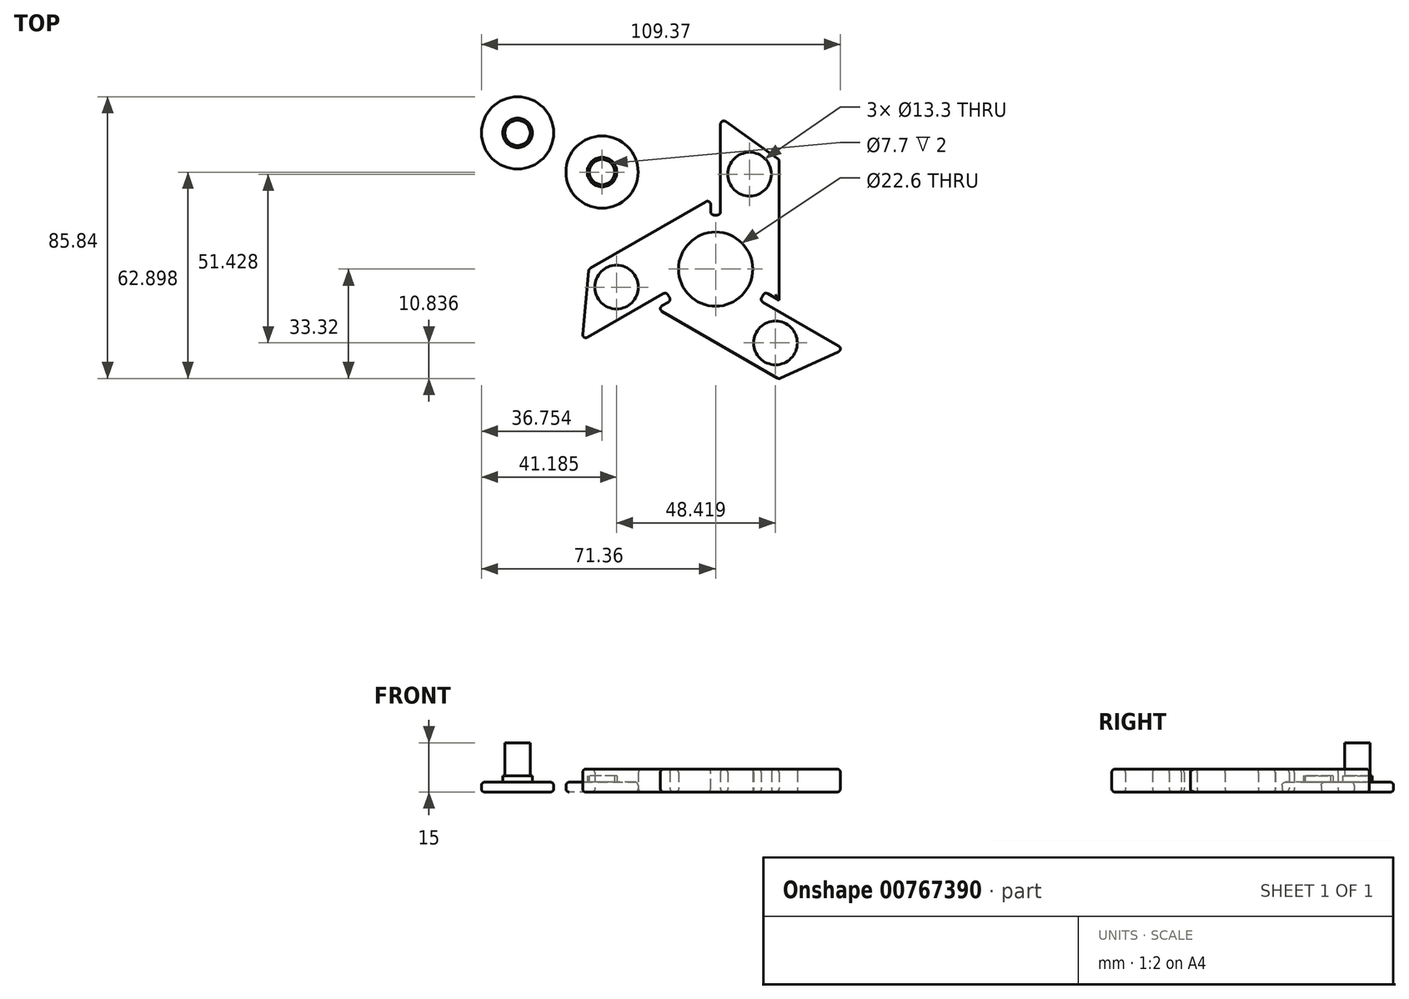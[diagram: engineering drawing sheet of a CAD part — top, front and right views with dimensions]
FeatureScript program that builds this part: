
annotation { "Feature Type Name" : "Feature", "Feature Type Description" : "" }
export const myFeature = defineFeature(function(context is Context, id is Id, definition is map)
    precondition{}
    {
        {
            var Q0;
            Q0=qCreatedBy(makeId("Top.planeOp"),FACE);
            var sketch = newSketch(context, id + "F0", { "sketchPlane" : qUnion([Q0])});
            skCircle(sketch, "E0", {"center": v(0, 0) * mm, "radius": 11.3 * mm});
            skCircle(sketch, "E1", {"center": v(0, 0) * mm, "radius": 16.5 * mm});
            skLineSegment(sketch, "E2", {"start": v(0, 74) * mm, "end": v(0, -68.77) * mm, "construction": true});
            skLineSegment(sketch, "E3", {"start": v(0, 0) * mm, "end": v(71.6, -41.34) * mm, "construction": true});
            skLineSegment(sketch, "E4", {"start": v(0, 0) * mm, "end": v(-62.65, -36.17) * mm, "construction": true});
            skLineSegment(sketch, "E5", {"start": v(-1.5, 16.43) * mm, "end": v(-1.5, 21.43) * mm});
            skLineSegment(sketch, "E6", {"start": v(1.5, 16.43) * mm, "end": v(1.5, 21.43) * mm});
            skLineSegment(sketch, "E7", {"start": v(13.48, -9.51) * mm, "end": v(17.81, -12.01) * mm});
            skLineSegment(sketch, "E8", {"start": v(14.98, -6.92) * mm, "end": v(19.31, -9.42) * mm});
            skLineSegment(sketch, "E9", {"start": v(-13.48, -9.51) * mm, "end": v(-17.81, -12.01) * mm});
            skLineSegment(sketch, "E10", {"start": v(-14.98, -6.92) * mm, "end": v(-19.31, -9.42) * mm});
            skLineSegment(sketch, "E11", {"start": v(-1.5, 21.43) * mm, "end": v(-38.62, 0) * mm});
            skLineSegment(sketch, "E12", {"start": v(-38.62, 0) * mm, "end": v(-40.7, -21.76) * mm});
            skLineSegment(sketch, "E13", {"start": v(-40.7, -21.76) * mm, "end": v(-19.31, -9.42) * mm});
            skLineSegment(sketch, "E14", {"start": v(-17.81, -12.01) * mm, "end": v(19.31, -33.45) * mm});
            skLineSegment(sketch, "E15", {"start": v(19.31, -33.45) * mm, "end": v(39.2, -24.36) * mm});
            skLineSegment(sketch, "E16", {"start": v(39.2, -24.36) * mm, "end": v(17.81, -12.01) * mm});
            skLineSegment(sketch, "E17", {"start": v(19.31, -9.42) * mm, "end": v(19.31, 33.45) * mm});
            skLineSegment(sketch, "E18", {"start": v(19.31, 33.45) * mm, "end": v(1.5, 46.12) * mm});
            skLineSegment(sketch, "E19", {"start": v(1.5, 46.12) * mm, "end": v(1.5, 21.43) * mm});
            skCircle(sketch, "E20", {"center": v(-30.18, -5.47) * mm, "radius": 6.65 * mm});
            skCircle(sketch, "E21", {"center": v(18.24, -22.48) * mm, "radius": 6.65 * mm});
            skCircle(sketch, "E22", {"center": v(10.35, 28.94) * mm, "radius": 6.65 * mm});
            skCircle(sketch, "E23", {"center": v(-60.36, 41.52) * mm, "radius": 11 * mm});
            skCircle(sketch, "E24", {"center": v(-34.6, 29.58) * mm, "radius": 11 * mm});
            skSolve(sketch);
        }
        {
            var Q0;
            {var subQ1=sQuery(id+"F0.wireOp",EDGE,"E7");Q0=makeQuery(id+"F0.imprint","IMPRINT",FACE,{"disambiguationData":[TD([[makeQuery(id+"F0.imprint","IMPRINT",EDGE,{"derivedFrom":subQ1}),-1.0]])]});}
            var Q1;
            {var subQ0=sQuery(id+"F0.wireOp",EDGE,"E5");Q1=makeQuery(id+"F0.imprint","IMPRINT",FACE,{"disambiguationData":[TD([[makeQuery(id+"F0.imprint","IMPRINT",EDGE,{"derivedFrom":subQ0}),1.0]])]});}
            var Q2;
            {var subQ0=sQuery(id+"F0.wireOp",EDGE,"E6");Q2=makeQuery(id+"F0.imprint","IMPRINT",FACE,{"disambiguationData":[TD([[makeQuery(id+"F0.imprint","IMPRINT",EDGE,{"derivedFrom":subQ0}),-1.0]])]});}
            var Q3;
            Q3=makeQuery(id+"F0.imprint","IMPRINT",FACE,{"disambiguationData":[TD([[makeQuery(id+"F0.imprint","IMPRINT",EDGE,{"derivedFrom":sQuery(id+"F0.wireOp",EDGE,"E0")}),-1.0]])]});
            extrude(context, id + "F1", {"entities" : qUnion([Q0, Q1, Q2, Q3]), "depth" : 7 * mm, "offsetDistance" : 25 * mm});
        }
        {
            var Q0;
            Q0=makeQuery(id+"F1.opExtrude","CAP_EDGE",EDGE,{"disambiguationData":[OSD([sQuery(id+"F0.wireOp",EDGE,"E17")])],"isStart":false});
            var Q1;
            Q1=makeQuery(id+"F1.opExtrude","CAP_EDGE",EDGE,{"disambiguationData":[OSD([sQuery(id+"F0.wireOp",EDGE,"E18")])],"isStart":false});
            var Q2;
            Q2=makeQuery(id+"F1.opExtrude","CAP_EDGE",EDGE,{"disambiguationData":[OSD([sQuery(id+"F0.wireOp",EDGE,"E6"),sQuery(id+"F0.wireOp",EDGE,"E19")])],"isStart":false});
            var Q3;
            Q3=makeQuery(id+"F1.opExtrude","CAP_EDGE",EDGE,{"disambiguationData":[OSD([sQuery(id+"F0.wireOp",EDGE,"E11")])],"isStart":false});
            var Q4;
            Q4=makeQuery(id+"F1.opExtrude","CAP_EDGE",EDGE,{"disambiguationData":[OSD([sQuery(id+"F0.wireOp",EDGE,"E5")])],"isStart":false});
            var Q5;
            {var subQ0=sQuery(id+"F0.wireOp",EDGE,"E1");Q5=makeQuery(id+"F1.opExtrude","CAP_EDGE",EDGE,{"disambiguationData":[OSD([subQ0]),TDD([makeQuery(id+"F0.imprint","IMPRINT",EDGE,{"disambiguationData":[TD([[makeQuery(id+"F0.imprint","INTERSECT",VERTEX,{"derivedFrom":[subQ0,sQuery(id+"F0.wireOp",EDGE,"E5")]}),1.0]])],"derivedFrom":subQ0})])],"isStart":false});}
            var Q6;
            Q6=makeQuery(id+"F1.opExtrude","CAP_EDGE",EDGE,{"disambiguationData":[OSD([sQuery(id+"F0.wireOp",EDGE,"E12")])],"isStart":false});
            var Q7;
            Q7=makeQuery(id+"F1.opExtrude","CAP_EDGE",EDGE,{"disambiguationData":[OSD([sQuery(id+"F0.wireOp",EDGE,"E10"),sQuery(id+"F0.wireOp",EDGE,"E13")])],"isStart":false});
            var Q8;
            {var subQ0=sQuery(id+"F0.wireOp",EDGE,"E1");Q8=makeQuery(id+"F1.opExtrude","CAP_EDGE",EDGE,{"disambiguationData":[OSD([subQ0]),TDD([makeQuery(id+"F0.imprint","IMPRINT",EDGE,{"disambiguationData":[TD([[makeQuery(id+"F0.imprint","INTERSECT",VERTEX,{"derivedFrom":[subQ0,sQuery(id+"F0.wireOp",EDGE,"E9")]}),1.0]])],"derivedFrom":subQ0})])],"isStart":false});}
            var Q9;
            Q9=makeQuery(id+"F1.opExtrude","CAP_EDGE",EDGE,{"disambiguationData":[OSD([sQuery(id+"F0.wireOp",EDGE,"E9")])],"isStart":false});
            var Q10;
            Q10=makeQuery(id+"F1.opExtrude","CAP_EDGE",EDGE,{"disambiguationData":[OSD([sQuery(id+"F0.wireOp",EDGE,"E14")])],"isStart":false});
            var Q11;
            Q11=makeQuery(id+"F1.opExtrude","CAP_EDGE",EDGE,{"disambiguationData":[OSD([sQuery(id+"F0.wireOp",EDGE,"E15")])],"isStart":false});
            var Q12;
            Q12=makeQuery(id+"F1.opExtrude","CAP_EDGE",EDGE,{"disambiguationData":[OSD([sQuery(id+"F0.wireOp",EDGE,"E7"),sQuery(id+"F0.wireOp",EDGE,"E16")])],"isStart":false});
            var Q13;
            Q13=makeQuery(id+"F1.opExtrude","CAP_EDGE",EDGE,{"disambiguationData":[OSD([sQuery(id+"F0.wireOp",EDGE,"E8")])],"isStart":false});
            var Q14;
            Q14=makeQuery(id+"F1.opExtrude","CAP_EDGE",EDGE,{"disambiguationData":[OSD([sQuery(id+"F0.wireOp",EDGE,"E15")])],"isStart":true});
            var Q15;
            Q15=makeQuery(id+"F1.opExtrude","CAP_EDGE",EDGE,{"disambiguationData":[OSD([sQuery(id+"F0.wireOp",EDGE,"E14")])],"isStart":true});
            var Q16;
            Q16=makeQuery(id+"F1.opExtrude","SWEPT_EDGE",EDGE,{"disambiguationData":[OSD([sQuery(id+"F0.wireOp",EDGE,"E14"),sQuery(id+"F0.wireOp",EDGE,"E15")])]});
            var Q17;
            Q17=makeQuery(id+"F1.opExtrude","SWEPT_EDGE",EDGE,{"disambiguationData":[OSD([sQuery(id+"F0.wireOp",EDGE,"E15"),sQuery(id+"F0.wireOp",EDGE,"E16")])]});
            var Q18;
            Q18=makeQuery(id+"F1.opExtrude","SWEPT_EDGE",EDGE,{"disambiguationData":[OSD([sQuery(id+"F0.wireOp",EDGE,"E9"),sQuery(id+"F0.wireOp",EDGE,"E14")])]});
            var Q19;
            Q19=makeQuery(id+"F1.opExtrude","SWEPT_EDGE",EDGE,{"disambiguationData":[OSD([sQuery(id+"F0.wireOp",EDGE,"E1"),sQuery(id+"F0.wireOp",EDGE,"E10")])]});
            var Q20;
            Q20=makeQuery(id+"F1.opExtrude","SWEPT_EDGE",EDGE,{"disambiguationData":[OSD([sQuery(id+"F0.wireOp",EDGE,"E1"),sQuery(id+"F0.wireOp",EDGE,"E9")])]});
            var Q21;
            Q21=makeQuery(id+"F1.opExtrude","CAP_EDGE",EDGE,{"disambiguationData":[OSD([sQuery(id+"F0.wireOp",EDGE,"E10"),sQuery(id+"F0.wireOp",EDGE,"E13")])],"isStart":true});
            var Q22;
            Q22=makeQuery(id+"F1.opExtrude","SWEPT_EDGE",EDGE,{"disambiguationData":[OSD([sQuery(id+"F0.wireOp",EDGE,"E12"),sQuery(id+"F0.wireOp",EDGE,"E13")])]});
            var Q23;
            Q23=makeQuery(id+"F1.opExtrude","CAP_EDGE",EDGE,{"disambiguationData":[OSD([sQuery(id+"F0.wireOp",EDGE,"E12")])],"isStart":true});
            var Q24;
            Q24=makeQuery(id+"F1.opExtrude","SWEPT_EDGE",EDGE,{"disambiguationData":[OSD([sQuery(id+"F0.wireOp",EDGE,"E11"),sQuery(id+"F0.wireOp",EDGE,"E12")])]});
            var Q25;
            Q25=makeQuery(id+"F1.opExtrude","CAP_EDGE",EDGE,{"disambiguationData":[OSD([sQuery(id+"F0.wireOp",EDGE,"E11")])],"isStart":true});
            var Q26;
            Q26=makeQuery(id+"F1.opExtrude","SWEPT_EDGE",EDGE,{"disambiguationData":[OSD([sQuery(id+"F0.wireOp",EDGE,"E5"),sQuery(id+"F0.wireOp",EDGE,"E11")])]});
            var Q27;
            Q27=makeQuery(id+"F1.opExtrude","SWEPT_EDGE",EDGE,{"disambiguationData":[OSD([sQuery(id+"F0.wireOp",EDGE,"E1"),sQuery(id+"F0.wireOp",EDGE,"E5")])]});
            var Q28;
            Q28=makeQuery(id+"F1.opExtrude","SWEPT_EDGE",EDGE,{"disambiguationData":[OSD([sQuery(id+"F0.wireOp",EDGE,"E1"),sQuery(id+"F0.wireOp",EDGE,"E6")])]});
            var Q29;
            Q29=makeQuery(id+"F1.opExtrude","CAP_EDGE",EDGE,{"disambiguationData":[OSD([sQuery(id+"F0.wireOp",EDGE,"E6"),sQuery(id+"F0.wireOp",EDGE,"E19")])],"isStart":true});
            var Q30;
            Q30=makeQuery(id+"F1.opExtrude","SWEPT_EDGE",EDGE,{"disambiguationData":[OSD([sQuery(id+"F0.wireOp",EDGE,"E18"),sQuery(id+"F0.wireOp",EDGE,"E19")])]});
            var Q31;
            Q31=makeQuery(id+"F1.opExtrude","CAP_EDGE",EDGE,{"disambiguationData":[OSD([sQuery(id+"F0.wireOp",EDGE,"E18")])],"isStart":true});
            var Q32;
            Q32=makeQuery(id+"F1.opExtrude","SWEPT_EDGE",EDGE,{"disambiguationData":[OSD([sQuery(id+"F0.wireOp",EDGE,"E17"),sQuery(id+"F0.wireOp",EDGE,"E18")])]});
            var Q33;
            Q33=makeQuery(id+"F1.opExtrude","CAP_EDGE",EDGE,{"disambiguationData":[OSD([sQuery(id+"F0.wireOp",EDGE,"E17")])],"isStart":true});
            var Q34;
            Q34=makeQuery(id+"F1.opExtrude","SWEPT_EDGE",EDGE,{"disambiguationData":[OSD([sQuery(id+"F0.wireOp",EDGE,"E1"),sQuery(id+"F0.wireOp",EDGE,"E7")])]});
            var Q35;
            Q35=makeQuery(id+"F1.opExtrude","CAP_EDGE",EDGE,{"disambiguationData":[OSD([sQuery(id+"F0.wireOp",EDGE,"E7"),sQuery(id+"F0.wireOp",EDGE,"E16")])],"isStart":true});
            var Q36;
            Q36=makeQuery(id+"F1.opExtrude","SWEPT_EDGE",EDGE,{"disambiguationData":[OSD([sQuery(id+"F0.wireOp",EDGE,"E1"),sQuery(id+"F0.wireOp",EDGE,"E8")])]});
            var Q37;
            Q37=makeQuery(id+"F1.opExtrude","CAP_EDGE",EDGE,{"disambiguationData":[OSD([sQuery(id+"F0.wireOp",EDGE,"E8")])],"isStart":true});
            var Q38;
            {var subQ0=sQuery(id+"F0.wireOp",EDGE,"E1");Q38=makeQuery(id+"F1.opExtrude","CAP_EDGE",EDGE,{"disambiguationData":[OSD([subQ0]),TDD([makeQuery(id+"F0.imprint","IMPRINT",EDGE,{"disambiguationData":[TD([[makeQuery(id+"F0.imprint","INTERSECT",VERTEX,{"derivedFrom":[subQ0,sQuery(id+"F0.wireOp",EDGE,"E7")]}),-1.0]])],"derivedFrom":subQ0})])],"isStart":true});}
            var Q39;
            {var subQ0=sQuery(id+"F0.wireOp",EDGE,"E1");Q39=makeQuery(id+"F1.opExtrude","CAP_EDGE",EDGE,{"disambiguationData":[OSD([subQ0]),TDD([makeQuery(id+"F0.imprint","IMPRINT",EDGE,{"disambiguationData":[TD([[makeQuery(id+"F0.imprint","INTERSECT",VERTEX,{"derivedFrom":[subQ0,sQuery(id+"F0.wireOp",EDGE,"E7")]}),-1.0]])],"derivedFrom":subQ0})])],"isStart":false});}
            var Q40;
            Q40=makeQuery(id+"F1.opExtrude","CAP_EDGE",EDGE,{"disambiguationData":[OSD([sQuery(id+"F0.wireOp",EDGE,"E5")])],"isStart":true});
            var Q41;
            {var subQ0=sQuery(id+"F0.wireOp",EDGE,"E1");Q41=makeQuery(id+"F1.opExtrude","CAP_EDGE",EDGE,{"disambiguationData":[OSD([subQ0]),TDD([makeQuery(id+"F0.imprint","IMPRINT",EDGE,{"disambiguationData":[TD([[makeQuery(id+"F0.imprint","INTERSECT",VERTEX,{"derivedFrom":[subQ0,sQuery(id+"F0.wireOp",EDGE,"E5")]}),1.0]])],"derivedFrom":subQ0})])],"isStart":true});}
            var Q42;
            {var subQ0=sQuery(id+"F0.wireOp",EDGE,"E1");Q42=makeQuery(id+"F1.opExtrude","CAP_EDGE",EDGE,{"disambiguationData":[OSD([subQ0]),TDD([makeQuery(id+"F0.imprint","IMPRINT",EDGE,{"disambiguationData":[TD([[makeQuery(id+"F0.imprint","INTERSECT",VERTEX,{"derivedFrom":[subQ0,sQuery(id+"F0.wireOp",EDGE,"E9")]}),1.0]])],"derivedFrom":subQ0})])],"isStart":true});}
            var Q43;
            Q43=makeQuery(id+"F1.opExtrude","CAP_EDGE",EDGE,{"disambiguationData":[OSD([sQuery(id+"F0.wireOp",EDGE,"E9")])],"isStart":true});
            var Q44;
            Q44=makeQuery(id+"F1.opExtrude","CAP_EDGE",EDGE,{"disambiguationData":[OSD([sQuery(id+"F0.wireOp",EDGE,"E0")])],"isStart":false});
            var Q45;
            Q45=makeQuery(id+"F1.opExtrude","CAP_EDGE",EDGE,{"disambiguationData":[OSD([sQuery(id+"F0.wireOp",EDGE,"E21")])],"isStart":false});
            var Q46;
            Q46=makeQuery(id+"F1.opExtrude","CAP_EDGE",EDGE,{"disambiguationData":[OSD([sQuery(id+"F0.wireOp",EDGE,"E21")])],"isStart":true});
            var Q47;
            Q47=makeQuery(id+"F1.opExtrude","CAP_EDGE",EDGE,{"disambiguationData":[OSD([sQuery(id+"F0.wireOp",EDGE,"E20")])],"isStart":false});
            var Q48;
            Q48=makeQuery(id+"F1.opExtrude","CAP_EDGE",EDGE,{"disambiguationData":[OSD([sQuery(id+"F0.wireOp",EDGE,"E20")])],"isStart":true});
            var Q49;
            Q49=makeQuery(id+"F1.opExtrude","CAP_EDGE",EDGE,{"disambiguationData":[OSD([sQuery(id+"F0.wireOp",EDGE,"E22")])],"isStart":true});
            var Q50;
            Q50=makeQuery(id+"F1.opExtrude","CAP_EDGE",EDGE,{"disambiguationData":[OSD([sQuery(id+"F0.wireOp",EDGE,"E22")])],"isStart":false});
            var Q51;
            Q51=makeQuery(id+"F1.opExtrude","CAP_EDGE",EDGE,{"disambiguationData":[OSD([sQuery(id+"F0.wireOp",EDGE,"E0")])],"isStart":true});
            fillet(context, id + "F2", {"entities" : qUnion([Q0, Q1, Q2, Q3, Q4, Q5, Q6, Q7, Q8, Q9, Q10, Q11, Q12, Q13, Q14, Q15, Q16, Q17, Q18, Q19, Q20, Q21, Q22, Q23, Q24, Q25, Q26, Q27, Q28, Q29, Q30, Q31, Q32, Q33, Q34, Q35, Q36, Q37, Q38, Q39, Q40, Q41, Q42, Q43, Q44, Q45, Q46, Q47, Q48, Q49, Q50, Q51]), "radius" : 1 * mm, "tangentPropagation" : true, "allowEdgeOverflow" : false});
        }
        {
            var Q0;
            Q0=makeQuery(id+"F0.imprint","IMPRINT",FACE,{"disambiguationData":[TD([[makeQuery(id+"F0.imprint","IMPRINT",EDGE,{"derivedFrom":sQuery(id+"F0.wireOp",EDGE,"E24")}),1.0]])]});
            var Q1;
            Q1=makeQuery(id+"F0.imprint","IMPRINT",FACE,{"disambiguationData":[TD([[makeQuery(id+"F0.imprint","IMPRINT",EDGE,{"derivedFrom":sQuery(id+"F0.wireOp",EDGE,"E23")}),1.0]])]});
            extrude(context, id + "F3", {"entities" : qUnion([Q0, Q1]), "depth" : 3 * mm, "offsetDistance" : 25 * mm});
        }
        {
            var Q0;
            Q0=makeQuery(id+"F3.opExtrude","CAP_FACE",FACE,{"disambiguationData":[OSD([sQuery(id+"F0.wireOp",EDGE,"E23")])],"isStart":false});
            var sketch = newSketch(context, id + "F4", { "sketchPlane" : qUnion([Q0])});
            skCircle(sketch, "E25", {"center": v(-60.36, 41.52) * mm, "radius": 4.5 * mm});
            skSolve(sketch);
        }
        {
            var Q0;
            Q0 = qSketchRegion(id + "F4", true);
            extrude(context, id + "F5", {"entities" : qUnion([Q0]), "operationType" : NewBodyOperationType.ADD, "depth" : 2 * mm, "offsetDistance" : 25 * mm});
        }
        {
            var Q0;
            Q0=makeQuery(id+"F5.opExtrude","CAP_FACE",FACE,{"disambiguationData":[OSD([sQuery(id+"F4.wireOp",EDGE,"E25")])],"isStart":false});
            var sketch = newSketch(context, id + "F6", { "sketchPlane" : qUnion([Q0])});
            skCircle(sketch, "E26", {"center": v(-60.36, 41.52) * mm, "radius": 3.85 * mm});
            skSolve(sketch);
        }
        {
            var Q0;
            Q0 = qSketchRegion(id + "F6", true);
            extrude(context, id + "F7", {"entities" : qUnion([Q0]), "operationType" : NewBodyOperationType.ADD, "depth" : 10 * mm, "offsetDistance" : 25 * mm});
        }
        {
            var Q0;
            Q0=makeQuery(id+"F3.opExtrude","CAP_FACE",FACE,{"disambiguationData":[OSD([sQuery(id+"F0.wireOp",EDGE,"E24")])],"isStart":false});
            var sketch = newSketch(context, id + "F8", { "sketchPlane" : qUnion([Q0])});
            skCircle(sketch, "E27", {"center": v(-34.6, 29.58) * mm, "radius": 4.5 * mm});
            skSolve(sketch);
        }
        {
            var Q0;
            Q0 = qSketchRegion(id + "F8", true);
            extrude(context, id + "F9", {"entities" : qUnion([Q0]), "operationType" : NewBodyOperationType.ADD, "depth" : 2 * mm, "offsetDistance" : 25 * mm});
        }
        {
            var Q0;
            Q0=makeQuery(id+"F9.opExtrude","CAP_FACE",FACE,{"disambiguationData":[OSD([sQuery(id+"F8.wireOp",EDGE,"E27")])],"isStart":false});
            var sketch = newSketch(context, id + "F10", { "sketchPlane" : qUnion([Q0])});
            skCircle(sketch, "E28", {"center": v(-34.6, 29.58) * mm, "radius": 3.85 * mm});
            skSolve(sketch);
        }
        {
            var Q0;
            Q0 = qSketchRegion(id + "F10", true);
            extrude(context, id + "F11", {"entities" : qUnion([Q0]), "operationType" : NewBodyOperationType.REMOVE, "oppositeDirection" : true, "depth" : 2 * mm, "offsetDistance" : 25 * mm});
        }
        {
            var Q0;
            Q0=makeQuery(id+"F3.opExtrude","CAP_EDGE",EDGE,{"disambiguationData":[OSD([sQuery(id+"F0.wireOp",EDGE,"E23")])],"isStart":true});
            var Q1;
            Q1=makeQuery(id+"F3.opExtrude","CAP_EDGE",EDGE,{"disambiguationData":[OSD([sQuery(id+"F0.wireOp",EDGE,"E24")])],"isStart":true});
            var Q2;
            Q2=makeQuery(id+"F3.opExtrude","CAP_EDGE",EDGE,{"disambiguationData":[OSD([sQuery(id+"F0.wireOp",EDGE,"E23")])],"isStart":false});
            var Q3;
            Q3=makeQuery(id+"F3.opExtrude","CAP_EDGE",EDGE,{"disambiguationData":[OSD([sQuery(id+"F0.wireOp",EDGE,"E24")])],"isStart":false});
            fillet(context, id + "F12", {"entities" : qUnion([Q0, Q1, Q2, Q3]), "radius" : 1 * mm, "tangentPropagation" : true, "allowEdgeOverflow" : false});
        }
    });
